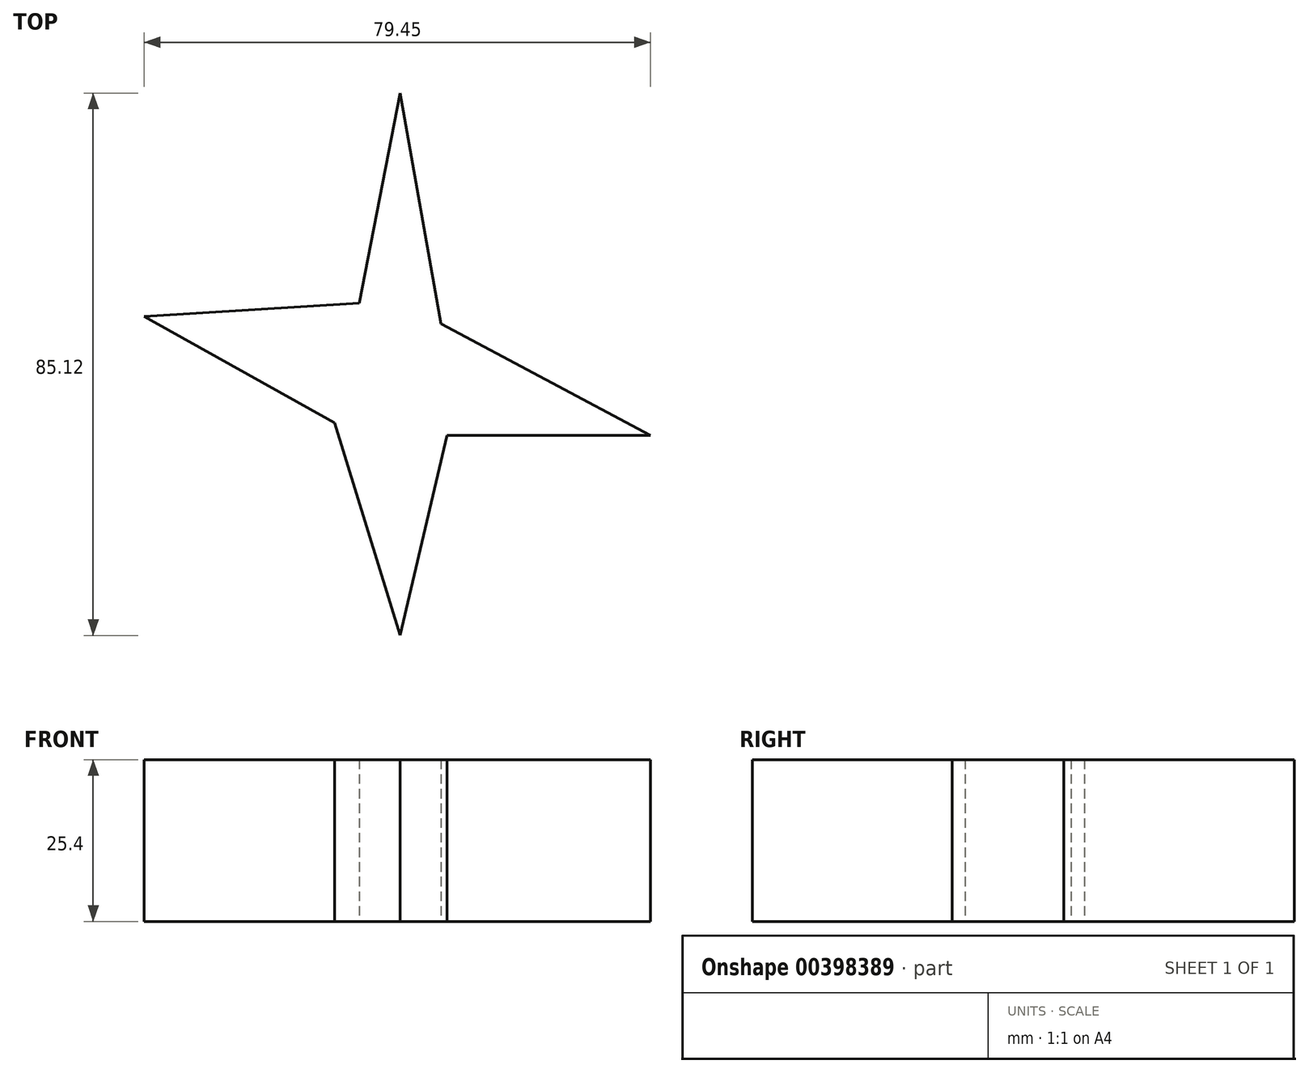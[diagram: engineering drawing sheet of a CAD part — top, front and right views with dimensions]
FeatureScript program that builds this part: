
annotation { "Feature Type Name" : "Feature", "Feature Type Description" : "" }
export const myFeature = defineFeature(function(context is Context, id is Id, definition is map)
    precondition{}
    {
        {
            var Q0;
            Q0=qCreatedBy(makeId("Top.planeOp"),FACE);
            var sketch = newSketch(context, id + "F0", { "sketchPlane" : qUnion([Q0])});
            skLineSegment(sketch, "E0", {"start": v(0, 0) * mm, "end": v(-40.16, 9.45) * mm});
            skLineSegment(sketch, "E1", {"start": v(0, 0) * mm, "end": v(0, 44.48) * mm});
            skLineSegment(sketch, "E2", {"start": v(0, 0) * mm, "end": v(39.29, -9.25) * mm});
            skLineSegment(sketch, "E3", {"start": v(0, 0) * mm, "end": v(0, -40.64) * mm});
            skLineSegment(sketch, "E4", {"start": v(-40.16, 9.45) * mm, "end": v(-10.27, -7.24) * mm});
            skLineSegment(sketch, "E5", {"start": v(-10.27, -7.24) * mm, "end": v(0, -40.64) * mm});
            skLineSegment(sketch, "E6", {"start": v(0, -40.64) * mm, "end": v(7.4, -9.21) * mm});
            skLineSegment(sketch, "E7", {"start": v(7.4, -9.21) * mm, "end": v(39.29, -9.25) * mm});
            skLineSegment(sketch, "E8", {"start": v(39.29, -9.25) * mm, "end": v(6.4, 8.26) * mm});
            skLineSegment(sketch, "E9", {"start": v(6.4, 8.26) * mm, "end": v(0, 44.48) * mm});
            skLineSegment(sketch, "E10", {"start": v(-6.4, 11.53) * mm, "end": v(0, 44.48) * mm});
            skLineSegment(sketch, "E11", {"start": v(-6.4, 11.53) * mm, "end": v(-40.16, 9.45) * mm});
            skSolve(sketch);
        }
        {
            var Q0;
            Q0=makeQuery(id+"F0.imprint","IMPRINT",FACE,{"disambiguationData":[TD([[makeQuery(id+"F0.imprint","IMPRINT",EDGE,{"derivedFrom":sQuery(id+"F0.wireOp",EDGE,"E0")}),1.0]])]});
            var Q1;
            Q1=makeQuery(id+"F0.imprint","IMPRINT",FACE,{"disambiguationData":[TD([[makeQuery(id+"F0.imprint","IMPRINT",EDGE,{"derivedFrom":sQuery(id+"F0.wireOp",EDGE,"E0")}),-1.0]])]});
            var Q2;
            Q2=makeQuery(id+"F0.imprint","IMPRINT",FACE,{"disambiguationData":[TD([[makeQuery(id+"F0.imprint","IMPRINT",EDGE,{"derivedFrom":sQuery(id+"F0.wireOp",EDGE,"E1")}),-1.0]])]});
            var Q3;
            Q3=makeQuery(id+"F0.imprint","IMPRINT",FACE,{"disambiguationData":[TD([[makeQuery(id+"F0.imprint","IMPRINT",EDGE,{"derivedFrom":sQuery(id+"F0.wireOp",EDGE,"E2")}),-1.0]])]});
            extrude(context, id + "F1", {"entities" : qUnion([Q0, Q1, Q2, Q3]), "depth" : 25.4 * mm});
        }
    });
